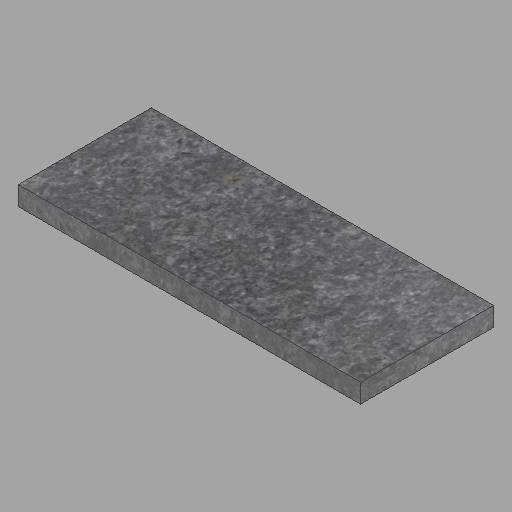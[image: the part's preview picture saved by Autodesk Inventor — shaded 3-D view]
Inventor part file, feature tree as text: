
AUTODESK INVENTOR PART (.ipt)
format: ipt  version: 2023 (Build 270158000, 158)  size: 221,696 bytes
history: native  units: in
note: dims shown in document units (in); Inventor stores cm internally (conversion verified against a paired STEP export)
features: other x1, extrude x1, sketch x1
ambient origin geometry x8: Origin, YZ Plane, XZ Plane, XY Plane, X Axis, Y Axis, Z Axis, Center Point
bodies: Solid1 (feature_tree)
feature tree (3):
  other  "2x14x36-18"
  extrude  "Extrusion1"  Depth=14.0in
  sketch  "Sketch1"  dims[d0=2.0in d1=14.0in d2=36.0in d3=0.0in]
